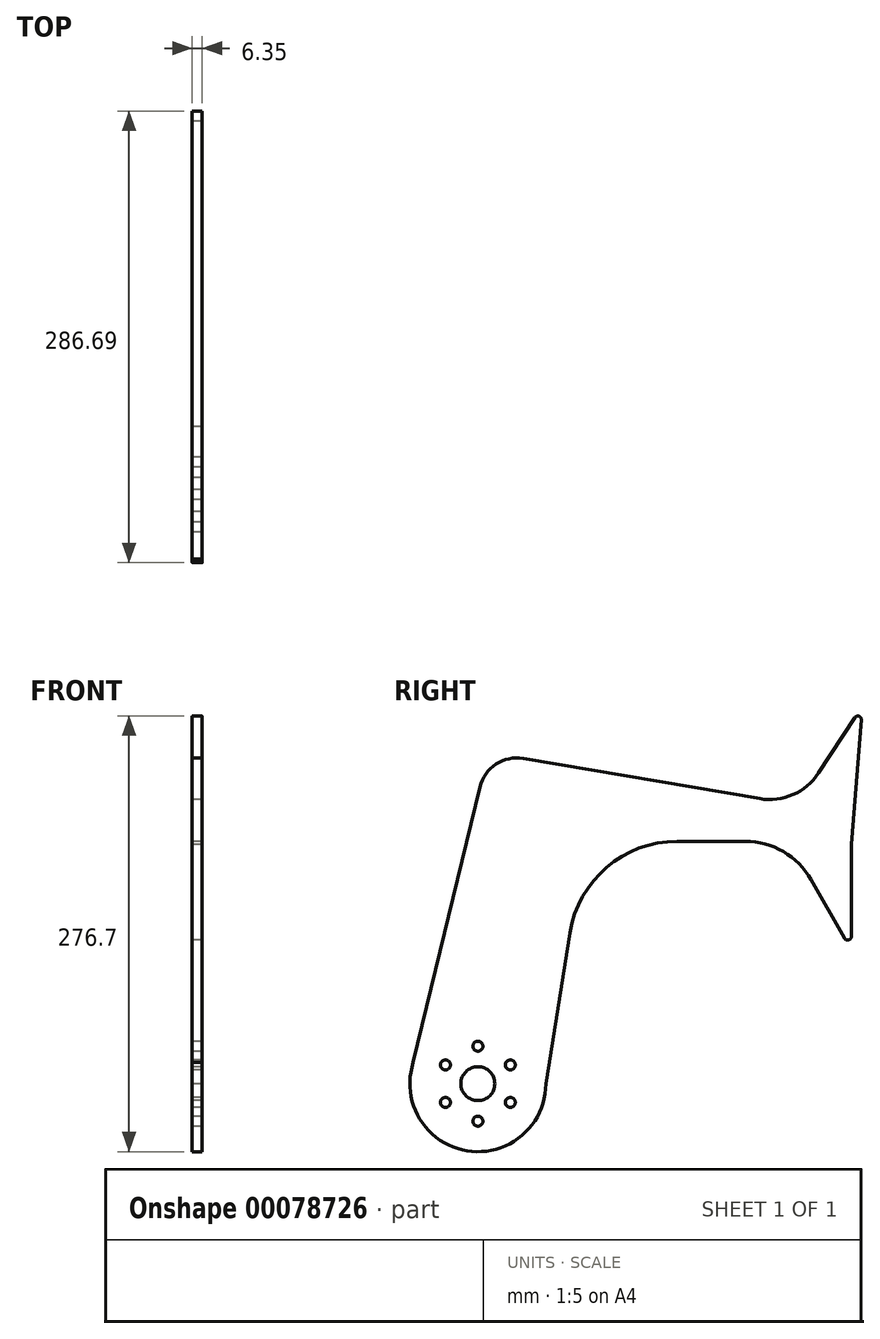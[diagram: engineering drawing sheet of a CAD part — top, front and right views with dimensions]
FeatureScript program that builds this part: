
annotation { "Feature Type Name" : "Feature", "Feature Type Description" : "" }
export const myFeature = defineFeature(function(context is Context, id is Id, definition is map)
    precondition{}
    {
        {
            var Q0;
            Q0=qCreatedBy(makeId("Right.planeOp"),FACE);
            var sketch = newSketch(context, id + "F0", { "sketchPlane" : qUnion([Q0])});
            skLineSegment(sketch, "E0", {"start": v(-1.58, -154.12) * mm, "end": v(13.68, -58.14) * mm});
            skLineSegment(sketch, "E1", {"start": v(81.8, 0) * mm, "end": v(125.08, 0) * mm});
            skLineSegment(sketch, "E2", {"start": v(192.24, -5.59) * mm, "end": v(198.72, 77.24) * mm});
            skLineSegment(sketch, "E3", {"start": v(194.77, 78.6) * mm, "end": v(171.56, 43.28) * mm});
            skLineSegment(sketch, "E4", {"start": v(134.32, 27.08) * mm, "end": v(-15.85, 52.61) * mm});
            skLineSegment(sketch, "E5", {"start": v(-43.44, 34.44) * mm, "end": v(-85.83, -140.54) * mm});
            skPoint(sketch, "E6.visualSharp", {"position": v(192.68, 0) * mm});
            skPoint(sketch, "E7.visualSharp", {"position": v(22.93, 0) * mm});
            skArc(sketch, "E7.filletArc", {"start": v(81.8, 0) * mm, "mid": v(37.02, -16.51) * mm, "end": v(13.68, -58.14) * mm});
            skPoint(sketch, "E8.visualSharp", {"position": v(-38.12, 56.4) * mm});
            skArc(sketch, "E8.filletArc", {"start": v(-15.85, 52.61) * mm, "mid": v(-33.22, 48.96) * mm, "end": v(-43.44, 34.44) * mm});
            skPoint(sketch, "E9.visualSharp", {"position": v(158.23, 23.01) * mm});
            skArc(sketch, "E9.filletArc", {"start": v(134.32, 27.08) * mm, "mid": v(155.35, 29.64) * mm, "end": v(171.56, 43.28) * mm});
            skLineSegment(sketch, "E10", {"start": v(192.51, 0) * mm, "end": v(192.51, -60.3) * mm});
            skLineSegment(sketch, "E11", {"start": v(187.9, -61.52) * mm, "end": v(166.87, -24.37) * mm});
            skPoint(sketch, "E12", {"position": v(137.16, 0) * mm});
            skPoint(sketch, "E13.visualSharp", {"position": v(-18.27, -259) * mm});
            skPoint(sketch, "E14.visualSharp", {"position": v(-112.45, -250.43) * mm});
            skPoint(sketch, "E15.newPointA", {"position": v(153.08, 0) * mm});
            skPoint(sketch, "E15.newPointB", {"position": v(192.51, 0) * mm});
            skArc(sketch, "E15.filletArc", {"start": v(166.87, -24.37) * mm, "mid": v(149.27, -6.54) * mm, "end": v(125.08, 0) * mm});
            skPoint(sketch, "E16.visualSharp", {"position": v(199.38, 85.6) * mm});
            skArc(sketch, "E16.filletArc", {"start": v(198.72, 77.24) * mm, "mid": v(197.27, 79.45) * mm, "end": v(194.77, 78.6) * mm});
            skPoint(sketch, "E17.visualSharp", {"position": v(192.51, -69.7) * mm});
            skArc(sketch, "E17.filletArc", {"start": v(192.48, -69.63) * mm, "mid": v(192.5, -69.64) * mm, "end": v(192.51, -69.62) * mm});
            skArc(sketch, "E18.filletArc", {"start": v(187.9, -61.52) * mm, "mid": v(190.67, -62.7) * mm, "end": v(192.51, -60.3) * mm});
            skCircle(sketch, "E19", {"center": v(-44.77, -153.95) * mm, "radius": 43.19 * mm});
            skCircle(sketch, "E20", {"center": v(-44.77, -153.95) * mm, "radius": 10.77 * mm});
            skPoint(sketch, "E21", {"position": v(-44.77, -130.14) * mm});
            skPoint(sketch, "E22.1.0", {"position": v(-65.4, -142.04) * mm});
            skPoint(sketch, "E22.2.0", {"position": v(-65.4, -165.86) * mm});
            skPoint(sketch, "E22.3.0", {"position": v(-44.77, -177.76) * mm});
            skPoint(sketch, "E22.4.0", {"position": v(-24.15, -165.86) * mm});
            skPoint(sketch, "E22.5.0", {"position": v(-24.15, -142.04) * mm});
            skSolve(sketch);
        }
        {
            var Q0;
            Q0=makeQuery(id+"F0.imprint","IMPRINT",FACE,{"disambiguationData":[TD([[makeQuery(id+"F0.imprint","IMPRINT",EDGE,{"derivedFrom":sQuery(id+"F0.wireOp",EDGE,"E0")}),1.0]])]});
            extrude(context, id + "F1", {"entities" : qUnion([Q0]), "depth" : 6.35 * mm});
        }
        {
            var Q0;
            {var subQ0=sQuery(id+"F0.wireOp",EDGE,"E10");Q0=makeQuery(id+"F0.imprint","IMPRINT",FACE,{"disambiguationData":[TD([[makeQuery(id+"F0.imprint","IMPRINT",EDGE,{"derivedFrom":subQ0}),-1.0]])]});}
            extrude(context, id + "F2", {"entities" : qUnion([Q0]), "operationType" : NewBodyOperationType.ADD, "depth" : 6.35 * mm});
        }
        {
            var Q0;
            Q0=makeQuery(id+"F1.opExtrude","CAP_FACE",FACE,{"disambiguationData":[OSD([sQuery(id+"F0.wireOp",EDGE,"E0"),sQuery(id+"F0.wireOp",EDGE,"E1"),sQuery(id+"F0.wireOp",EDGE,"E2"),sQuery(id+"F0.wireOp",EDGE,"E3"),sQuery(id+"F0.wireOp",EDGE,"E4"),sQuery(id+"F0.wireOp",EDGE,"E5"),sQuery(id+"F0.wireOp",EDGE,"E7.filletArc"),sQuery(id+"F0.wireOp",EDGE,"E8.filletArc"),sQuery(id+"F0.wireOp",EDGE,"E9.filletArc"),sQuery(id+"F0.wireOp",EDGE,"e1bb0cd2-49ca-4208-82d9-40ad98cda44d"),sQuery(id+"F0.wireOp",EDGE,"E10"),sQuery(id+"F0.wireOp",EDGE,"E11"),sQuery(id+"F0.wireOp",EDGE,"UkPQ0f5z-xmOE-aKsi-LPIj-pIVzT7c7XED3"),sQuery(id+"F0.wireOp",EDGE,"E13.filletArc"),sQuery(id+"F0.wireOp",EDGE,"E14.filletArc"),sQuery(id+"F0.wireOp",EDGE,"E15.filletArc")])],"isStart":false});
            var sketch = newSketch(context, id + "F3", { "sketchPlane" : qUnion([Q0])});
            skCircle(sketch, "E23", {"center": v(236.52, 16.45) * mm, "radius": 6.35 * mm});
            skSolve(sketch);
        }
        {
            var Q0;
            Q0=sQuery(id+"F3.wireOp",VERTEX,"E23.center");
            var Q1;
            Q1=makeQuery(id+"F1.opExtrude","SWEPT_BODY",BODY,{"disambiguationData":[OSD([sQuery(id+"F0.wireOp",EDGE,"E0"),sQuery(id+"F0.wireOp",EDGE,"E1"),sQuery(id+"F0.wireOp",EDGE,"E2"),sQuery(id+"F0.wireOp",EDGE,"E3"),sQuery(id+"F0.wireOp",EDGE,"E4"),sQuery(id+"F0.wireOp",EDGE,"E5"),sQuery(id+"F0.wireOp",EDGE,"E7.filletArc"),sQuery(id+"F0.wireOp",EDGE,"E8.filletArc"),sQuery(id+"F0.wireOp",EDGE,"E9.filletArc"),sQuery(id+"F0.wireOp",EDGE,"e1bb0cd2-49ca-4208-82d9-40ad98cda44d"),sQuery(id+"F0.wireOp",EDGE,"E10"),sQuery(id+"F0.wireOp",EDGE,"E11"),sQuery(id+"F0.wireOp",EDGE,"UkPQ0f5z-xmOE-aKsi-LPIj-pIVzT7c7XED3"),sQuery(id+"F0.wireOp",EDGE,"E13.filletArc"),sQuery(id+"F0.wireOp",EDGE,"E14.filletArc"),sQuery(id+"F0.wireOp",EDGE,"E15.filletArc")])]});
            hole(context, id + "F4", {"style" : HoleStyle.SIMPLE, "endStyle" : HoleEndStyle.THROUGH, "holeDiameter" : 25.4 * mm, "locations" : qUnion([Q0]), "scope" : qUnion([Q1]), "isTappedThrough" : true});
        }
        {
            var Q0;
            Q0=makeQuery(id+"F0.imprint","IMPRINT",FACE,{"disambiguationData":[TD([[makeQuery(id+"F0.imprint","IMPRINT",EDGE,{"derivedFrom":sQuery(id+"F0.wireOp",EDGE,"E20")}),-1.0]])]});
            extrude(context, id + "F5", {"entities" : qUnion([Q0]), "operationType" : NewBodyOperationType.ADD, "depth" : 6.35 * mm});
        }
        {
            var Q0;
            Q0=sQuery(id+"F0.wireOp",VERTEX,"E21");
            var Q1;
            Q1=sQuery(id+"F0.wireOp",VERTEX,"E22.5.0");
            var Q2;
            Q2=sQuery(id+"F0.wireOp",VERTEX,"E22.4.0");
            var Q3;
            Q3=sQuery(id+"F0.wireOp",VERTEX,"E22.3.0");
            var Q4;
            Q4=sQuery(id+"F0.wireOp",VERTEX,"E22.2.0");
            var Q5;
            Q5=sQuery(id+"F0.wireOp",VERTEX,"E22.1.0");
            var Q6;
            Q6=makeQuery(id+"F1.opExtrude","SWEPT_BODY",BODY,{"disambiguationData":[OSD([sQuery(id+"F0.wireOp",EDGE,"E0"),sQuery(id+"F0.wireOp",EDGE,"E1"),sQuery(id+"F0.wireOp",EDGE,"E2"),sQuery(id+"F0.wireOp",EDGE,"E3"),sQuery(id+"F0.wireOp",EDGE,"E4"),sQuery(id+"F0.wireOp",EDGE,"E5"),sQuery(id+"F0.wireOp",EDGE,"E7.filletArc"),sQuery(id+"F0.wireOp",EDGE,"E8.filletArc"),sQuery(id+"F0.wireOp",EDGE,"E9.filletArc"),sQuery(id+"F0.wireOp",EDGE,"E10"),sQuery(id+"F0.wireOp",EDGE,"E11"),sQuery(id+"F0.wireOp",EDGE,"E15.filletArc"),sQuery(id+"F0.wireOp",EDGE,"E16.filletArc"),sQuery(id+"F0.wireOp",EDGE,"E18.filletArc"),sQuery(id+"F0.wireOp",EDGE,"E19")])]});
            hole(context, id + "F6", {"style" : HoleStyle.SIMPLE, "endStyle" : HoleEndStyle.THROUGH, "oppositeDirection" : true, "holeDiameter" : 6.35 * mm, "locations" : qUnion([Q0, Q1, Q2, Q3, Q4, Q5]), "scope" : qUnion([Q6]), "isTappedThrough" : true});
        }
    });
